# Revit family: IS_Hotline_K2770_BIM_DE
name_source: partatom
category: Plumbing Fixtures
revit_build: Autodesk Revit MEP 2016 (Build: 20161004_0715(x64)
units: mm (PartAtom-declared; Revit-internal decimal feet)

## family parameters
Always vertical = No
Cut with Voids When Loaded = No
OmniClass Number = 23.45.05.14.21.11
OmniClass Title = Bath/Shower Units
Part Type = Normal
Room Calculation Point = No
Round Connector Dimension = Use Diameter
Shared = No
Work Plane-Based = No

## types (1)
- K277001 - HOTLINE NEU rectangular shower tray 900x800mm
    Accessories = www.idealstandard.de\ersatzteile
    AssetType = Fixed
    BIMObjectName = ISI_IdealStandard_ShowerTrays_Hotline_K277001
    BIMobject category = Shower trays
    BOSUseNativeGeometries = 1
    BarCode = 4015413057868
    Brand = Ideal Standard
    Brand url = http://www.idealstandard.de
    CodePerformance = DIN EN 14527, DIN EN 251, DIN EN
    Color = White
    ConnectionType = Plumbing
    Cost = 0 $
    CurrencyUnit = €
    CurrentRevision = 1
    Date of publishing = 20/12/2017
    Description = IS Rechteck-Brausewanne HOTLINE NEU, 900x800x145mm, Weiß
    DrainSize = 0 mm  [stored 0 ft]
    DurationUnit = Year
    EAN code = https://4015413057868
    Edition number = 1
    ExpectedLife = 25
    Features = IS Rechteck-Brausewanne HOTLINE NEU, 900x800x145mm, Weiß
    Finish = White
    IFC Classification = Sanitary Terminal
    IfcExportAs = IfcSanitaryTerminalType
    Installation instructions = http://www.idealstandard.de
    InstallationInstructions = www.idealstandard.de\produkte
    MainColor = White
    MaintenanceInformation = www.idealstandard.de\produkte
    Manufacturer name = Ideal Standard
    ManufacturerURL = http://www.idealstandard.de
    Material = Sanitary Brass
    Material main = Acrylic
    MaterialThickness = 0 mm  [stored 0 ft]
    Model = K277001
    ModelNumber = K277001
    ModelReference = IS Rechteck-Brausewanne HOTLINE NEU, 900x800x145mm, Weiß
    NBS Reference Code = 35-06-84
    NBS Reference Description = Shower Trays
    Name = ShowerTrays_Hotline_K277001
    NettWeight = 14 Kg
    Nominal height = 145
    Nominal width = 800
    NominalDepth = 800 mm  [stored 2.62467 ft]
    NominalHeight = 140 mm
    NominalLength = 800 mm  [stored 2.62467 ft]
    NominalWidth = 900 mm
    OmniClass Code = 23-31 17 00
    OmniClass Description = Showers
    Product Guid = 4964503e-e743-40ee-b0a5-d611cf871764
    Product SKU = K2770
    Product data url = https://bimobject.com
    Product family = Sanitary
    Product group = Shower Tray
    Product name = HOTLINE NEU rectangular shower tray 900x800mm
    Product url = http://www.idealstandard.de
    ProductInformation = www.idealstandard.de/produkte
    QR code = http://bimobject.com
    Shape = Rectangular
    Size = 140 x 800 x 900mm
    Space = Internal
    SpareParts = www.idealstandard.de/ersatzteile
    Technical description = http://www.idealstandard.de
    URL = http://www.idealstandard.de
    Uniclass 1.4 Code = L7214
    Uniclass 1.4 Description = Showers
    Uniclass 2.0 Code = PR-35-06-84
    Uniclass 2.0 Description = Shower Trays
    Uniclass 2015 Code = Pr_40_20_06_84
    Uniclass 2015 Name = Shower trays
    Uniclass2015Code = Pr_40_20_06_84
    Uniclass2015Title = Shower trays
    Uniclass2015Version = Products v1.1
    Version = 1
    VolumeUnits = Litres
    Weight Net (Kg) = 14

note: [stored X ft] marks values corroborated as IEEE doubles in the binary element streams (Revit-internal decimal feet)

## geometry (parser evidence)
native form markers: Blend x4, Sweep x1
no freeform markers — native parametric forms only
